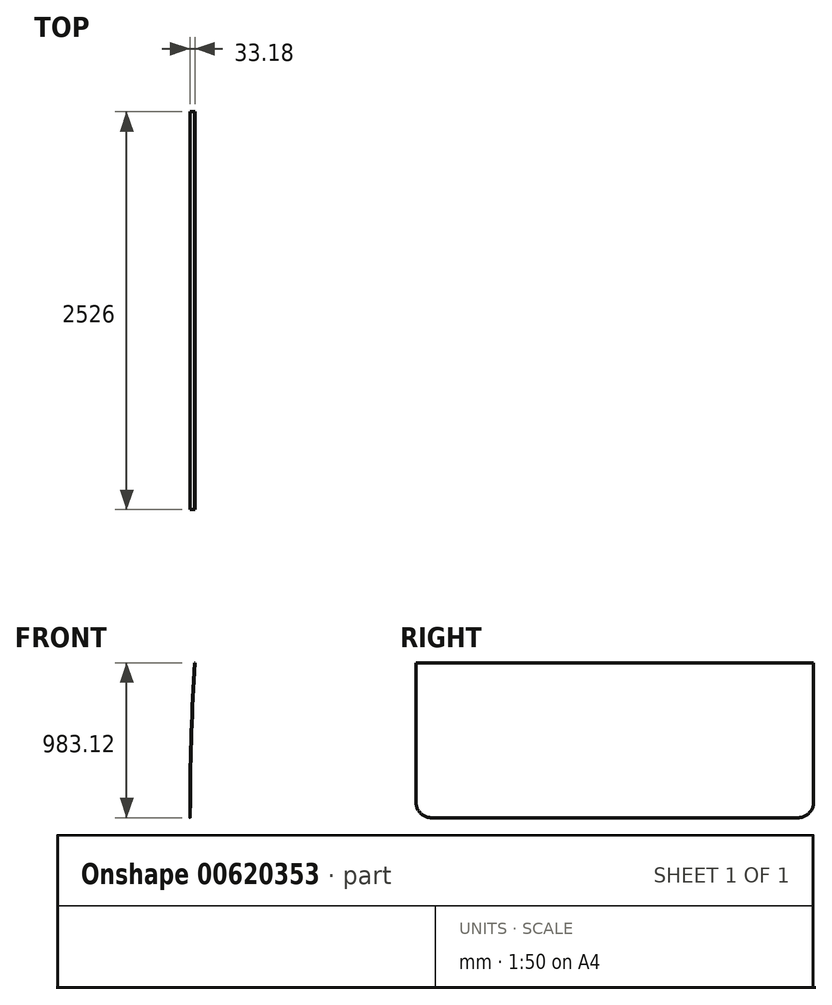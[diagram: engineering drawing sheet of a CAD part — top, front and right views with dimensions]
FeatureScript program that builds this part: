
annotation { "Feature Type Name" : "Feature", "Feature Type Description" : "" }
export const myFeature = defineFeature(function(context is Context, id is Id, definition is map)
    precondition{}
    {
        {
            var Q0;
            Q0=qCreatedBy(makeId("Front.planeOp"),FACE);
            var sketch = newSketch(context, id + "F0", { "sketchPlane" : qUnion([Q0])});
            skLineSegment(sketch, "E0", {"start": v(-685, 0) * mm, "end": v(685, 0) * mm, "construction": true});
            skLineSegment(sketch, "E1", {"start": v(-640, 1400) * mm, "end": v(640, 1400) * mm, "construction": true});
            skArc(sketch, "E2", {"start": v(414.68, 1458.6) * mm, "mid": v(0, 1500) * mm, "end": v(-414.68, 1458.6) * mm, "construction": true});
            skLineSegment(sketch, "E3", {"start": v(0, 1500) * mm, "end": v(0, 0) * mm, "construction": true});
            skPoint(sketch, "E3.endSnap0", {"position": v(0, 1500) * mm});
            skLineSegment(sketch, "E4", {"start": v(-685, 0) * mm, "end": v(-685, 200) * mm, "construction": true});
            skLineSegment(sketch, "E5", {"start": v(685, 0) * mm, "end": v(685, 200) * mm, "construction": true});
            skLineSegment(sketch, "E6", {"start": v(-685, 200) * mm, "end": v(685, 200) * mm, "construction": true});
            skArc(sketch, "E7", {"start": v(-654.82, 1182.93) * mm, "mid": v(-677.45, 691.7) * mm, "end": v(-685, 200) * mm});
            skArc(sketch, "E8", {"start": v(685, 200) * mm, "mid": v(677.45, 691.7) * mm, "end": v(654.82, 1182.93) * mm, "construction": true});
            skPoint(sketch, "E9.visualSharp", {"position": v(-640, 1400) * mm});
            skArc(sketch, "E9.filletArc", {"start": v(-414.68, 1458.6) * mm, "mid": v(-581.6, 1361.58) * mm, "end": v(-654.82, 1182.93) * mm, "construction": true});
            skPoint(sketch, "E10.visualSharp", {"position": v(640, 1400) * mm});
            skArc(sketch, "E10.filletArc", {"start": v(654.82, 1182.93) * mm, "mid": v(581.6, 1361.58) * mm, "end": v(414.68, 1458.6) * mm, "construction": true});
            skPoint(sketch, "E11", {"position": v(0, 1400) * mm});
            skArc(sketch, "E12.0", {"start": v(-657.82, 1183.12) * mm, "mid": v(-680.45, 691.79) * mm, "end": v(-688, 200) * mm});
            skLineSegment(sketch, "E13", {"start": v(-657.82, 1183.12) * mm, "end": v(-654.82, 1182.93) * mm});
            skLineSegment(sketch, "E14", {"start": v(-688, 200) * mm, "end": v(-685, 200) * mm});
            skSolve(sketch);
        }
        {
            var Q0;
            Q0=makeQuery(id+"F0.imprint","IMPRINT",FACE,{"disambiguationData":[TD([[makeQuery(id+"F0.imprint","IMPRINT",EDGE,{"derivedFrom":sQuery(id+"F0.wireOp",EDGE,"E0")}),1.0]])]});
            var Q1;
            Q1=makeQuery(id+"F0.imprint","IMPRINT",FACE,{"disambiguationData":[TD([[makeQuery(id+"F0.imprint","IMPRINT",EDGE,{"derivedFrom":sQuery(id+"F0.wireOp",EDGE,"E2")}),-1.0]])]});
            var Q2;
            Q2=makeQuery(id+"F0.imprint","IMPRINT",FACE,{"disambiguationData":[TD([[makeQuery(id+"F0.imprint","IMPRINT",EDGE,{"derivedFrom":sQuery(id+"F0.wireOp",EDGE,"E7")}),-1.0]])]});
            extrude(context, id + "F1", {"entities" : qUnion([Q0, Q1, Q2]), "depth" : 2526 * mm, "offsetDistance" : 25 * mm});
        }
        {
            var Q0;
            Q0=makeQuery(id+"F1.opExtrude","CAP_EDGE",EDGE,{"disambiguationData":[OSD([sQuery(id+"F0.wireOp",EDGE,"E14")])],"isStart":false});
            var Q1;
            Q1=makeQuery(id+"F1.opExtrude","CAP_EDGE",EDGE,{"disambiguationData":[OSD([sQuery(id+"F0.wireOp",EDGE,"E14")])],"isStart":true});
            fillet(context, id + "F2", {"entities" : qUnion([Q0, Q1]), "radius" : 100 * mm, "tangentPropagation" : true, "allowEdgeOverflow" : false});
        }
    });
